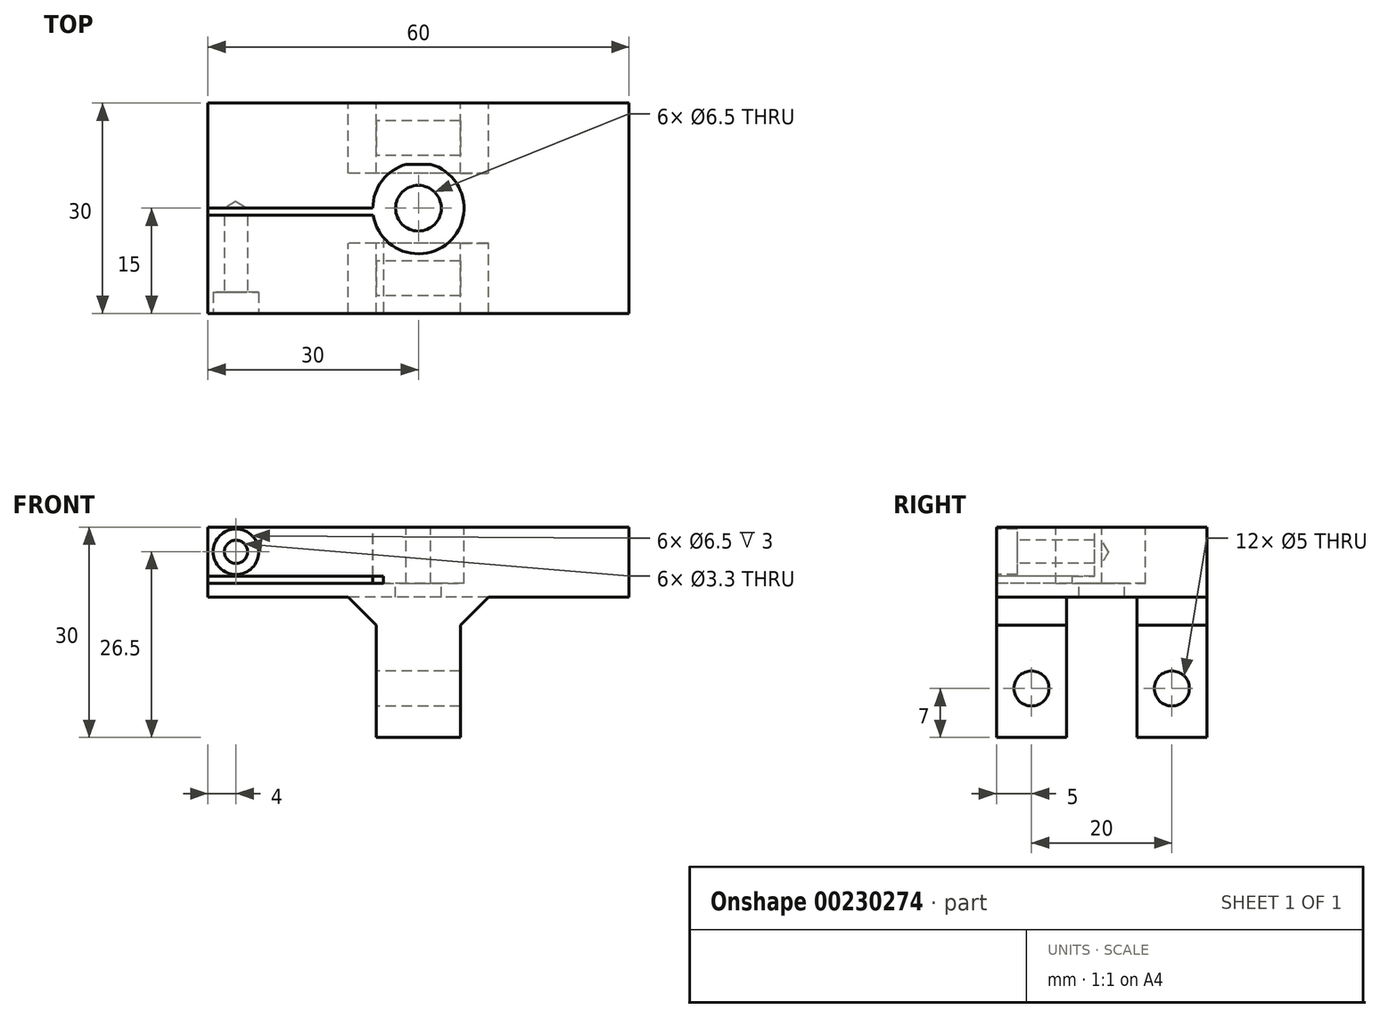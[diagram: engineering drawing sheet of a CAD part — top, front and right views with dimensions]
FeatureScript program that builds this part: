
annotation { "Feature Type Name" : "Feature", "Feature Type Description" : "" }
export const myFeature = defineFeature(function(context is Context, id is Id, definition is map)
    precondition{}
    {
        {
            var Q0;
            Q0=qCreatedBy(makeId("Front.planeOp"),FACE);
            var sketch = newSketch(context, id + "F0", { "sketchPlane" : qUnion([Q0])});
            skLineSegment(sketch, "E0", {"start": v(-6, 0) * mm, "end": v(-6, 16) * mm});
            skLineSegment(sketch, "E1", {"start": v(-6, 16) * mm, "end": v(-10, 20) * mm});
            skLineSegment(sketch, "E2", {"start": v(-10, 20) * mm, "end": v(-30, 20) * mm});
            skLineSegment(sketch, "E3", {"start": v(-30, 20) * mm, "end": v(-30, 30) * mm});
            skLineSegment(sketch, "E4", {"start": v(-30, 30) * mm, "end": v(0, 30) * mm});
            skLineSegment(sketch, "E5", {"start": v(0, 30) * mm, "end": v(0, 0) * mm});
            skLineSegment(sketch, "E6", {"start": v(0, 0) * mm, "end": v(-6, 0) * mm});
            skLineSegment(sketch, "E7.MirrorCS", {"start": v(0, 0) * mm, "end": v(6, 0) * mm});
            skLineSegment(sketch, "E8.MirrorCS", {"start": v(6, 0) * mm, "end": v(6, 16) * mm});
            skLineSegment(sketch, "E9.MirrorCS", {"start": v(6, 16) * mm, "end": v(10, 20) * mm});
            skLineSegment(sketch, "E10.MirrorCS", {"start": v(10, 20) * mm, "end": v(30, 20) * mm});
            skLineSegment(sketch, "E11.MirrorCS", {"start": v(30, 30) * mm, "end": v(0, 30) * mm});
            skLineSegment(sketch, "E12.MirrorCS", {"start": v(30, 20) * mm, "end": v(30, 30) * mm});
            skSolve(sketch);
        }
        {
            var Q0;
            Q0=makeQuery(id+"F0.imprint","IMPRINT",FACE,{"disambiguationData":[TD([[makeQuery(id+"F0.imprint","IMPRINT",EDGE,{"derivedFrom":sQuery(id+"F0.wireOp",EDGE,"E0")}),-1.0]])]});
            var Q1;
            Q1=makeQuery(id+"F0.imprint","IMPRINT",FACE,{"disambiguationData":[TD([[makeQuery(id+"F0.imprint","IMPRINT",EDGE,{"derivedFrom":sQuery(id+"F0.wireOp",EDGE,"E5")}),1.0]])]});
            extrude(context, id + "F1", {"entities" : qUnion([Q0, Q1]), "endBound" : BoundingType.SYMMETRIC, "depth" : 30 * mm});
        }
        {
            var Q0;
            Q0=makeQuery(id+"F1.opExtrude","SWEPT_FACE",FACE,{"disambiguationData":[OSD([sQuery(id+"F0.wireOp",EDGE,"E4"),sQuery(id+"F0.wireOp",EDGE,"E11.MirrorCS")])]});
            var sketch = newSketch(context, id + "F2", { "sketchPlane" : qUnion([Q0])});
            skArc(sketch, "E13", {"start": v(-1.75, 6.26) * mm, "mid": v(0, -6.5) * mm, "end": v(1.75, 6.26) * mm});
            skLineSegment(sketch, "E14", {"start": v(-1.75, 6.26) * mm, "end": v(1.75, 6.26) * mm});
            skSolve(sketch);
        }
        {
            var Q0;
            Q0=makeQuery(id+"F2.imprint","IMPRINT",FACE,{"disambiguationData":[TD([[makeQuery(id+"F2.imprint","IMPRINT",EDGE,{"derivedFrom":sQuery(id+"F2.wireOp",EDGE,"E13")}),1.0]])]});
            extrude(context, id + "F3", {"entities" : qUnion([Q0]), "operationType" : NewBodyOperationType.REMOVE, "oppositeDirection" : true, "depth" : 8 * mm});
        }
        {
            var Q0;
            Q0=makeQuery(id+"F3.boolean.opBoolean","COPY",FACE,{"derivedFrom":makeQuery(id+"F3.opExtrude","CAP_FACE",FACE,{"disambiguationData":[OSD([sQuery(id+"F2.wireOp",EDGE,"E13"),sQuery(id+"F2.wireOp",EDGE,"E14")])],"isStart":false})});
            var sketch = newSketch(context, id + "F4", { "sketchPlane" : qUnion([Q0])});
            skCircle(sketch, "E15", {"center": v(0, 0) * mm, "radius": 3.25 * mm});
            skSolve(sketch);
        }
        {
            var Q0;
            Q0=makeQuery(id+"F4.imprint","IMPRINT",FACE,{"disambiguationData":[TD([[makeQuery(id+"F4.imprint","IMPRINT",EDGE,{"derivedFrom":sQuery(id+"F4.wireOp",EDGE,"E15")}),1.0]])]});
            extrude(context, id + "F5", {"entities" : qUnion([Q0]), "operationType" : NewBodyOperationType.REMOVE, "endBound" : BoundingType.THROUGH_ALL, "oppositeDirection" : true, "depth" : 25 * mm});
        }
        {
            var Q0;
            Q0=makeQuery(id+"F1.opExtrude","SWEPT_FACE",FACE,{"disambiguationData":[OSD([sQuery(id+"F0.wireOp",EDGE,"E3")])]});
            var sketch = newSketch(context, id + "F6", { "sketchPlane" : qUnion([Q0])});
            skLineSegment(sketch, "E16.bottom", {"start": v(5, 0) * mm, "end": v(-5, 0) * mm});
            skLineSegment(sketch, "E16.top", {"start": v(5, 20) * mm, "end": v(-5, 20) * mm});
            skLineSegment(sketch, "E16.left", {"start": v(5, 0) * mm, "end": v(5, 20) * mm});
            skLineSegment(sketch, "E16.right", {"start": v(-5, 0) * mm, "end": v(-5, 20) * mm});
            skSolve(sketch);
        }
        {
            var Q0;
            Q0=makeQuery(id+"F6.imprint","IMPRINT",FACE,{"disambiguationData":[TD([[makeQuery(id+"F6.imprint","IMPRINT",EDGE,{"derivedFrom":sQuery(id+"F6.wireOp",EDGE,"E16.bottom")}),-1.0]])]});
            extrude(context, id + "F7", {"entities" : qUnion([Q0]), "operationType" : NewBodyOperationType.REMOVE, "endBound" : BoundingType.THROUGH_ALL, "oppositeDirection" : true, "depth" : 25 * mm});
        }
        {
            var Q0;
            Q0=makeQuery(id+"F1.opExtrude","CAP_FACE",FACE,{"disambiguationData":[OSD([sQuery(id+"F0.wireOp",EDGE,"E0"),sQuery(id+"F0.wireOp",EDGE,"E1"),sQuery(id+"F0.wireOp",EDGE,"E2"),sQuery(id+"F0.wireOp",EDGE,"E3"),sQuery(id+"F0.wireOp",EDGE,"E4"),sQuery(id+"F0.wireOp",EDGE,"E6"),sQuery(id+"F0.wireOp",EDGE,"E7.MirrorCS"),sQuery(id+"F0.wireOp",EDGE,"E8.MirrorCS"),sQuery(id+"F0.wireOp",EDGE,"E9.MirrorCS"),sQuery(id+"F0.wireOp",EDGE,"E10.MirrorCS"),sQuery(id+"F0.wireOp",EDGE,"E11.MirrorCS"),sQuery(id+"F0.wireOp",EDGE,"E12.MirrorCS")])],"isStart":false});
            var sketch = newSketch(context, id + "F8", { "sketchPlane" : qUnion([Q0])});
            skLineSegment(sketch, "E17.bottom", {"start": v(-30, 22) * mm, "end": v(-5, 22) * mm});
            skLineSegment(sketch, "E17.top", {"start": v(-30, 23) * mm, "end": v(-5, 23) * mm});
            skLineSegment(sketch, "E17.left", {"start": v(-30, 22) * mm, "end": v(-30, 23) * mm});
            skLineSegment(sketch, "E17.right", {"start": v(-5, 22) * mm, "end": v(-5, 23) * mm});
            skSolve(sketch);
        }
        {
            var Q0;
            Q0=makeQuery(id+"F8.imprint","IMPRINT",FACE,{"disambiguationData":[TD([[makeQuery(id+"F8.imprint","IMPRINT",EDGE,{"derivedFrom":sQuery(id+"F8.wireOp",EDGE,"E17.bottom")}),1.0]])]});
            extrude(context, id + "F9", {"entities" : qUnion([Q0]), "operationType" : NewBodyOperationType.REMOVE, "oppositeDirection" : true, "depth" : 15 * mm});
        }
        {
            var Q0;
            Q0=makeQuery(id+"F1.opExtrude","SWEPT_FACE",FACE,{"disambiguationData":[OSD([sQuery(id+"F0.wireOp",EDGE,"E3")])]});
            var sketch = newSketch(context, id + "F10", { "sketchPlane" : qUnion([Q0])});
            skLineSegment(sketch, "E18.bottom", {"start": v(0, 23) * mm, "end": v(1, 23) * mm});
            skLineSegment(sketch, "E18.top", {"start": v(0, 30) * mm, "end": v(1, 30) * mm});
            skLineSegment(sketch, "E18.left", {"start": v(0, 23) * mm, "end": v(0, 30) * mm});
            skLineSegment(sketch, "E18.right", {"start": v(1, 23) * mm, "end": v(1, 30) * mm});
            skSolve(sketch);
        }
        {
            var Q0;
            Q0=makeQuery(id+"F10.imprint","IMPRINT",FACE,{"disambiguationData":[TD([[makeQuery(id+"F10.imprint","IMPRINT",EDGE,{"derivedFrom":sQuery(id+"F10.wireOp",EDGE,"E18.bottom")}),1.0]])]});
            extrude(context, id + "F11", {"entities" : qUnion([Q0]), "operationType" : NewBodyOperationType.REMOVE, "oppositeDirection" : true, "depth" : 25 * mm});
        }
        {
            var Q0;
            Q0=makeQuery(id+"F1.opExtrude","CAP_FACE",FACE,{"disambiguationData":[OSD([sQuery(id+"F0.wireOp",EDGE,"E0"),sQuery(id+"F0.wireOp",EDGE,"E1"),sQuery(id+"F0.wireOp",EDGE,"E2"),sQuery(id+"F0.wireOp",EDGE,"E3"),sQuery(id+"F0.wireOp",EDGE,"E4"),sQuery(id+"F0.wireOp",EDGE,"E6"),sQuery(id+"F0.wireOp",EDGE,"E7.MirrorCS"),sQuery(id+"F0.wireOp",EDGE,"E8.MirrorCS"),sQuery(id+"F0.wireOp",EDGE,"E9.MirrorCS"),sQuery(id+"F0.wireOp",EDGE,"E10.MirrorCS"),sQuery(id+"F0.wireOp",EDGE,"E11.MirrorCS"),sQuery(id+"F0.wireOp",EDGE,"E12.MirrorCS")])],"isStart":false});
            var sketch = newSketch(context, id + "F12", { "sketchPlane" : qUnion([Q0])});
            skPoint(sketch, "E19", {"position": v(-26, 26.5) * mm});
            skSolve(sketch);
        }
        {
            var Q0;
            Q0=sQuery(id+"F12.wireOp",VERTEX,"E19");
            var Q1;
            Q1=makeQuery(id+"F1.opExtrude","SWEPT_BODY",BODY,{"disambiguationData":[OSD([sQuery(id+"F0.wireOp",EDGE,"E0"),sQuery(id+"F0.wireOp",EDGE,"E1"),sQuery(id+"F0.wireOp",EDGE,"E2"),sQuery(id+"F0.wireOp",EDGE,"E3"),sQuery(id+"F0.wireOp",EDGE,"E4"),sQuery(id+"F0.wireOp",EDGE,"E6"),sQuery(id+"F0.wireOp",EDGE,"E7.MirrorCS"),sQuery(id+"F0.wireOp",EDGE,"E8.MirrorCS"),sQuery(id+"F0.wireOp",EDGE,"E9.MirrorCS"),sQuery(id+"F0.wireOp",EDGE,"E10.MirrorCS"),sQuery(id+"F0.wireOp",EDGE,"E11.MirrorCS"),sQuery(id+"F0.wireOp",EDGE,"E12.MirrorCS")])]});
            hole(context, id + "F13", {"style" : HoleStyle.C_BORE, "endStyle" : HoleEndStyle.BLIND, "standardTappedOrClearance" : lookupTablePath({ "standard" : "ISO", "fit" : "Normal", "size" : "M3", "type" : "Clearance" }), "standardBlindInLast" : lookupTablePath({ "fit" : "Standard", "standard" : "ISO", "size" : "M3", "type" : "Clearance" }), "holeDiameter" : 3.3 * mm, "cBoreDiameter" : 6.5 * mm, "cBoreDepth" : 3 * mm, "holeDepth" : 15 * mm, "locations" : qUnion([Q0]), "scope" : qUnion([Q1])});
        }
        {
            var Q0;
            {var subQ3=sQuery(id+"F0.wireOp",EDGE,"E0");Q0=makeQuery(id+"F7.boolean.opBoolean","SPLIT",FACE,{"disambiguationData":[TD([makeQuery(id+"F7.opExtrude","SWEPT_FACE",FACE,{"disambiguationData":[OSD([sQuery(id+"F6.wireOp",EDGE,"E16.left")])]})])],"derivedFrom":makeQuery(id+"F1.opExtrude","SWEPT_FACE",FACE,{"disambiguationData":[OSD([subQ3])]})});}
            var sketch = newSketch(context, id + "F14", { "sketchPlane" : qUnion([Q0])});
            skPoint(sketch, "E20", {"position": v(10, 7) * mm});
            skPoint(sketch, "E21", {"position": v(-10, 7) * mm});
            skSolve(sketch);
        }
        {
            var Q0;
            Q0=sQuery(id+"F14.wireOp",VERTEX,"E21");
            var Q1;
            Q1=sQuery(id+"F14.wireOp",VERTEX,"E20");
            var Q2;
            Q2=makeQuery(id+"F1.opExtrude","SWEPT_BODY",BODY,{"disambiguationData":[OSD([sQuery(id+"F0.wireOp",EDGE,"E0"),sQuery(id+"F0.wireOp",EDGE,"E1"),sQuery(id+"F0.wireOp",EDGE,"E2"),sQuery(id+"F0.wireOp",EDGE,"E3"),sQuery(id+"F0.wireOp",EDGE,"E4"),sQuery(id+"F0.wireOp",EDGE,"E6"),sQuery(id+"F0.wireOp",EDGE,"E7.MirrorCS"),sQuery(id+"F0.wireOp",EDGE,"E8.MirrorCS"),sQuery(id+"F0.wireOp",EDGE,"E9.MirrorCS"),sQuery(id+"F0.wireOp",EDGE,"E10.MirrorCS"),sQuery(id+"F0.wireOp",EDGE,"E11.MirrorCS"),sQuery(id+"F0.wireOp",EDGE,"E12.MirrorCS")])]});
            hole(context, id + "F15", {"style" : HoleStyle.SIMPLE, "endStyle" : HoleEndStyle.THROUGH, "holeDiameter" : 5 * mm, "locations" : qUnion([Q0, Q1]), "scope" : qUnion([Q2]), "isTappedThrough" : true});
        }
    });
